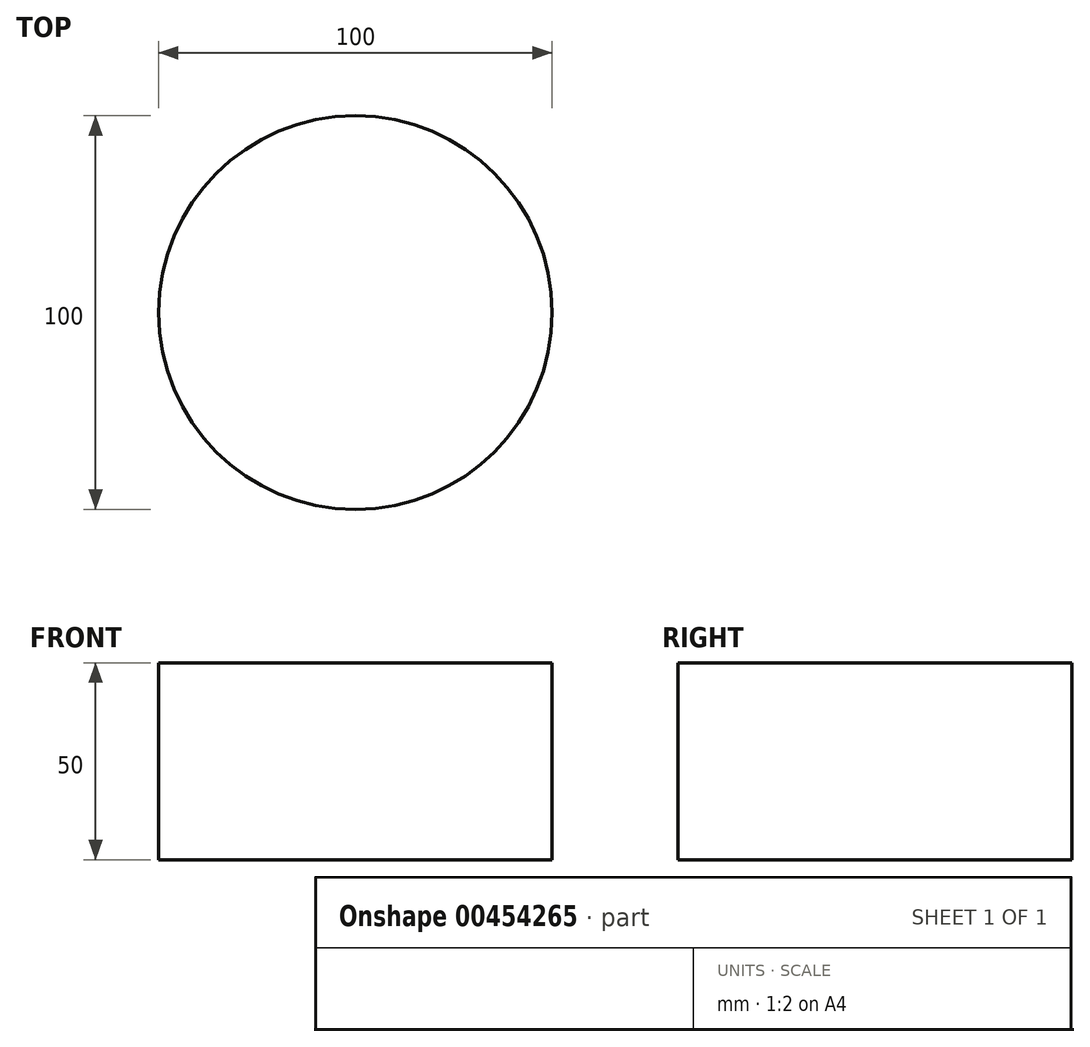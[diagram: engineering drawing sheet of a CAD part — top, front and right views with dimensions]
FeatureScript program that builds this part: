
annotation { "Feature Type Name" : "Feature", "Feature Type Description" : "" }
export const myFeature = defineFeature(function(context is Context, id is Id, definition is map)
    precondition{}
    {
        {
            var Q0;
            Q0=qCreatedBy(makeId("Top.planeOp"),FACE);
            var sketch = newSketch(context, id + "F0", { "sketchPlane" : qUnion([Q0])});
            skCircle(sketch, "E0", {"center": v(0, 0) * mm, "radius": 50 * mm});
            skSolve(sketch);
        }
        {
            var Q0;
            Q0=makeQuery(id+"F0.imprint","IMPRINT",FACE,{"disambiguationData":[TD([[makeQuery(id+"F0.imprint","IMPRINT",EDGE,{"derivedFrom":sQuery(id+"F0.wireOp",EDGE,"E0")}),1.0]])]});
            extrude(context, id + "F1", {"entities" : qUnion([Q0]), "depth" : 50 * mm});
        }
    });
